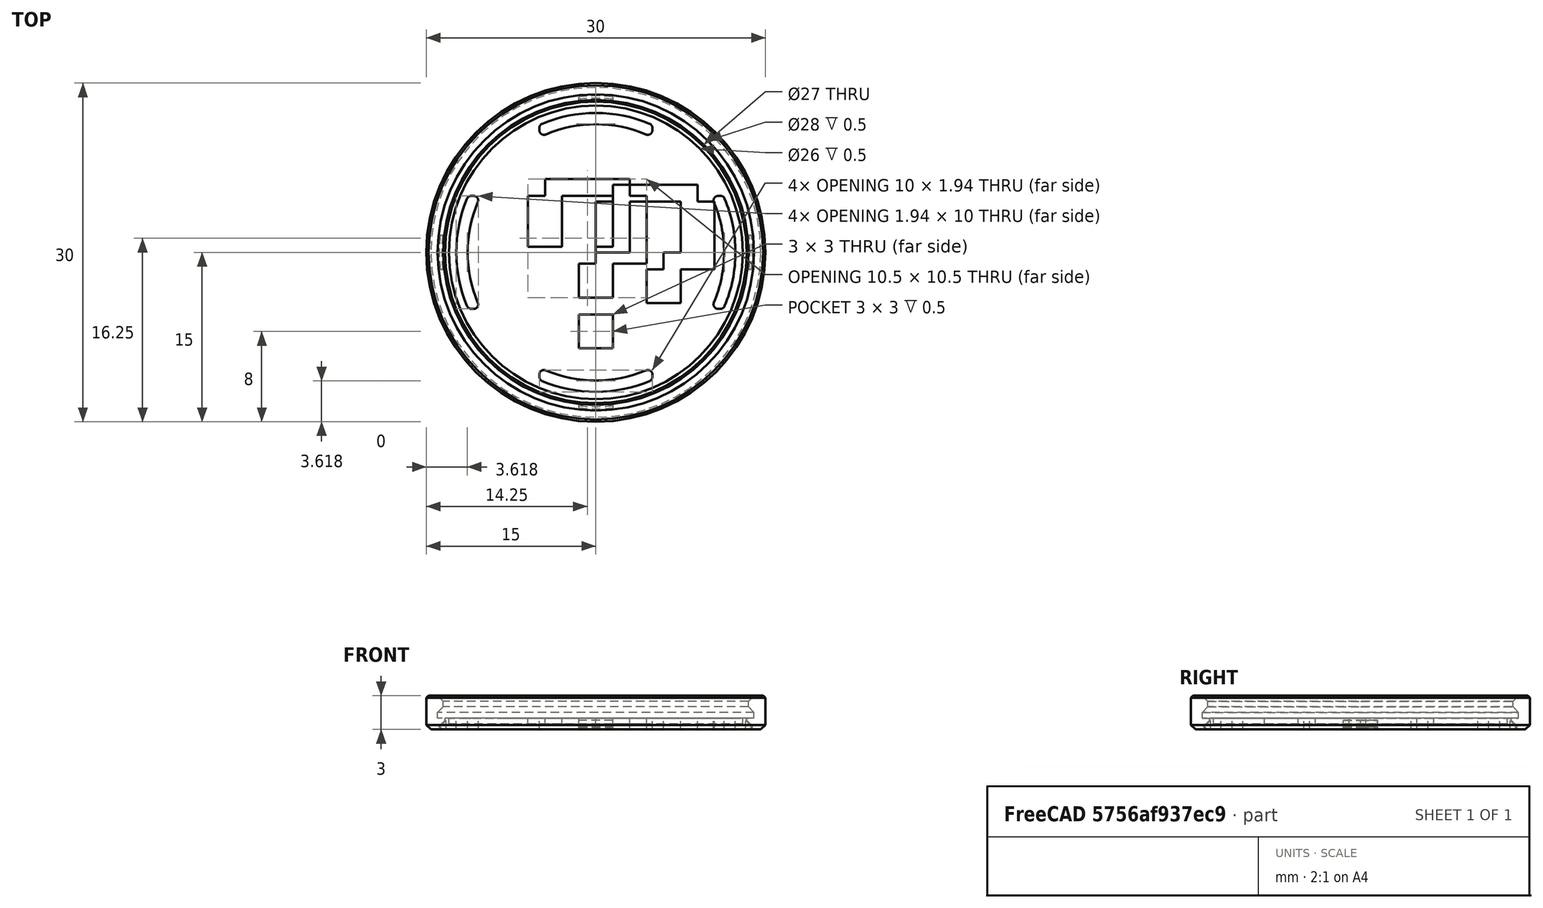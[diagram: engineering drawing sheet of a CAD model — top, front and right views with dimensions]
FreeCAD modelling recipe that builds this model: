
FCSTD DOCUMENT  (FreeCAD 0.18R16146 (Git))
Label: nfc-coin
License: All rights reserved
LicenseURL: http://en.wikipedia.org/wiki/All_rights_reserved
objects: Part::Cylinder×9, Part::MultiFuse×6, Part::Chamfer×6, Part::Cut×5, Part::Box×5, Part::Feature×3, Part::MultiCommon×2, Sketcher::SketchObject×1, PartDesign::Pad×1, PartDesign::Body×1, Part::Fillet×1
note: 41 computed .brp shape members not serialized (recipe doc carries the construction recipe); baked Part::Feature solids carry a one-line shape summary decoded from their .brp

FEATURE [Part::Cylinder] Cylinder
  Angle = 360
  AttacherType = Attacher::AttachEngine3D
  Height = 3
  Radius = 15
FEATURE [Part::Cylinder] Cylinder001
  Angle = 360
  AttacherType = Attacher::AttachEngine3D
  Height = 3
  Placement = pos=(0,0,0.5) rot=(0,0,1;0rad)
  Radius = 13
FEATURE [Part::Cylinder] Cylinder002
  Angle = 360
  AttacherType = Attacher::AttachEngine3D
  Height = 3
  Placement = pos=(0,0,1) rot=(0,0,1;0rad)
  Radius = 13.5
FEATURE [Part::MultiFuse] Fusion
  Shapes = -> [Cylinder002,Cylinder001]
FEATURE [Part::Cut] Cut
  Base = -> Cylinder
  Tool = -> Fusion
FEATURE [Part::Cylinder] Cylinder003
  Angle = 360
  AttacherType = Attacher::AttachEngine3D
  Height = 1
  Placement = pos=(0,0,1) rot=(0,0,1;0rad)
  Radius = 14
FEATURE [Part::Chamfer] Chamfer
  Base = -> Cylinder003
  Edges = 1 edges r=0.5: [Edge1]
FEATURE [Part::Cut] Cut001
  Base = -> Cut
  Tool = -> Chamfer
FEATURE [Part::Chamfer] Chamfer001
  Base = -> Cut001
  Edges = 1 edges r=0.5: [Edge4]
FEATURE [Part::Cylinder] Cylinder004
  Angle = 360
  AttacherType = Attacher::AttachEngine3D
  Height = 1
  Radius = 13.35
FEATURE [Part::Cylinder] Cylinder005
  Angle = 360
  AttacherType = Attacher::AttachEngine3D
  Height = 0.8
  Radius = 13.85
FEATURE [Part::Chamfer] Chamfer003
  Base = -> Cylinder005
  Edges = 1 edges r=0.5: [Edge1]
FEATURE [Part::Chamfer] Chamfer004
  Base = -> Chamfer003
  Edges = 1 edges r=0.2: [Edge3]
FEATURE [Part::Box] Box  label="Cube"
  AttacherType = Attacher::AttachEngine3D
  Height = 10
  Length = 28
  Placement = pos=(-14,-1.5,0) rot=(0,0,1;0rad)
  Width = 3
FEATURE [Part::Box] Box001  label="Cube001"
  AttacherType = Attacher::AttachEngine3D
  Height = 10
  Length = 3
  Placement = pos=(-1.5,-14,0) rot=(0,0,1;0rad)
  Width = 28
FEATURE [Part::MultiFuse] Fusion001
  Shapes = -> [Box,Box001]
FEATURE [Part::MultiCommon] Common
  Shapes = -> [Chamfer004,Fusion001]
FEATURE [Part::Cylinder] Cylinder006
  Angle = 360
  AttacherType = Attacher::AttachEngine3D
  Height = 10
  Radius = 12.35
FEATURE [Part::Cylinder] Cylinder007
  Angle = 360
  AttacherType = Attacher::AttachEngine3D
  Height = 10
  Radius = 11.35
FEATURE [Part::Cut] Cut002
  Base = -> Cylinder006
  Tool = -> Cylinder007
FEATURE [Part::Box] Box002  label="Cube002"
  AttacherType = Attacher::AttachEngine3D
  Height = 10
  Length = 28
  Placement = pos=(-14,-5,0) rot=(0,0,1;0rad)
  Width = 10
FEATURE [Part::Box] Box003  label="Cube003"
  AttacherType = Attacher::AttachEngine3D
  Height = 10
  Length = 10
  Placement = pos=(-5,-14,0) rot=(0,0,1;0rad)
  Width = 28
FEATURE [Part::MultiFuse] Fusion002
  Shapes = -> [Cylinder004,Common]
FEATURE [Part::MultiFuse] Fusion003
  Shapes = -> [Box002,Box003]
FEATURE [Part::MultiCommon] Common001
  Shapes = -> [Cut002,Fusion003]
FEATURE [Part::Cut] Cut003
  Base = -> Fusion002
  Tool = -> Common001
FEATURE [Sketcher::SketchObject] Sketch001
  MapMode = 5
  Support = -> [XY_Plane001]
  sketch-geometry (18):
    g0: LineSegment StartX=0 StartY=0 StartZ=0 EndX=0 EndY=4.5 EndZ=0
    g1: LineSegment StartX=0 StartY=4.5 StartZ=0 EndX=1.5 EndY=4.5 EndZ=0
    g2: LineSegment StartX=1.5 StartY=4.5 StartZ=0 EndX=1.5 EndY=6 EndZ=0
    g3: LineSegment StartX=1.5 StartY=6 StartZ=0 EndX=9 EndY=6 EndZ=0
    g4: LineSegment StartX=9 StartY=6 StartZ=0 EndX=9 EndY=4.5 EndZ=0
    g5: LineSegment StartX=9 StartY=4.5 StartZ=0 EndX=10.5 EndY=4.5 EndZ=0
    g6: LineSegment StartX=10.5 StartY=4.5 StartZ=0 EndX=10.5 EndY=-1.5 EndZ=0
    g7: LineSegment StartX=10.5 StartY=-1.5 StartZ=0 EndX=7.5 EndY=-1.5 EndZ=0
    g8: LineSegment StartX=7.5 StartY=-1.5 StartZ=0 EndX=7.5 EndY=-4.5 EndZ=0
    g9: LineSegment StartX=7.5 StartY=-4.5 StartZ=0 EndX=4.5 EndY=-4.5 EndZ=0
    g10: LineSegment StartX=4.5 StartY=-4.5 StartZ=0 EndX=4.5 EndY=-1.5 EndZ=0
    g11: LineSegment StartX=4.5 StartY=-1.5 StartZ=0 EndX=6 EndY=-1.5 EndZ=0
    g12: LineSegment StartX=6 StartY=-1.5 StartZ=0 EndX=6 EndY=0 EndZ=0
    g13: LineSegment StartX=6 StartY=0 StartZ=0 EndX=7.5 EndY=0 EndZ=0
    g14: LineSegment StartX=7.5 StartY=0 StartZ=0 EndX=7.5 EndY=4.5 EndZ=0
    g15: LineSegment StartX=7.5 StartY=4.5 StartZ=0 EndX=3 EndY=4.5 EndZ=0
    g16: LineSegment StartX=3 StartY=4.5 StartZ=0 EndX=3 EndY=0 EndZ=0
    g17: LineSegment StartX=3 StartY=0 StartZ=0 EndX=0 EndY=0 EndZ=0
  constraints (18):
    c: Coincident(g0,g1)
    c: Coincident(g1,g2)
    c: Coincident(g2,g3)
    c: Coincident(g3,g4)
    c: Coincident(g4,g5)
    c: Coincident(g5,g6)
    c: Coincident(g6,g7)
    c: Coincident(g7,g8)
    c: Coincident(g8,g9)
    c: Coincident(g9,g10)
    c: Coincident(g10,g11)
    c: Coincident(g11,g12)
    c: Coincident(g12,g13)
    c: Coincident(g13,g14)
    c: Coincident(g14,g15)
    c: Coincident(g15,g16)
    c: Coincident(g16,g17)
    c: Coincident(g17,g0)
FEATURE [PartDesign::Pad] Pad
  Length = 1
  Length2 = 100
  Profile = -> Sketch001
  Type = 0
FEATURE [PartDesign::Body] Body001
  Group = -> [Sketch001,Pad]
  Origin = -> Origin001
  Tip = -> Pad
FEATURE [Part::Feature] Body001001  label="Body002"
  shape: bbox 10.5 x 10.5 x 1 mm, 20 faces (baked)
FEATURE [Part::Box] Box004  label="Cube004"
  AttacherType = Attacher::AttachEngine3D
  Height = 1
  Length = 3
  Placement = pos=(4.5,-9,0) rot=(0,0,1;0rad)
  Width = 3
FEATURE [Part::MultiFuse] Fusion004
  Placement = pos=(-6,0.5,0.5) rot=(0,0,1;0rad)
  Shapes = -> [Body001001,Box004]
FEATURE [Part::Cut] Cut004
  Base = -> Cut003
  Tool = -> Fusion004
FEATURE [Part::Fillet] Fillet  label="top-question"
  Base = -> Cut004
  Edges = 16 edges r=0.4: [Edge147,Edge148,Edge149,Edge151,Edge156,Edge158,Edge166,Edge167,Edge168,Edge170,Edge176,Edge177,Edge178,Edge180,Edge184,Edge185]
FEATURE [Part::Chamfer] Chamfer005
  Base = -> Chamfer001
  Edges = 1 edges r=0.4: [Edge6]
FEATURE [Part::Chamfer] Chamfer006  label="bottom"
  Base = -> Chamfer005
  Edges = 1 edges r=0.2: [Edge3]
FEATURE [Part::Cylinder] Cylinder008
  Angle = 360
  AttacherType = Attacher::AttachEngine3D
  Height = 1
  Radius = 9
FEATURE [Part::Feature] Fillet001
  shape: bbox 27.7 x 27.7 x 1 mm, 100 faces (baked)
FEATURE [Part::MultiFuse] Fusion005
  Shapes = -> [Cylinder008,Fillet001]
FEATURE [Part::Feature] Fusion005001  label="blank-top"
  shape: bbox 27.7 x 27.7 x 1 mm, 57 faces (baked)
